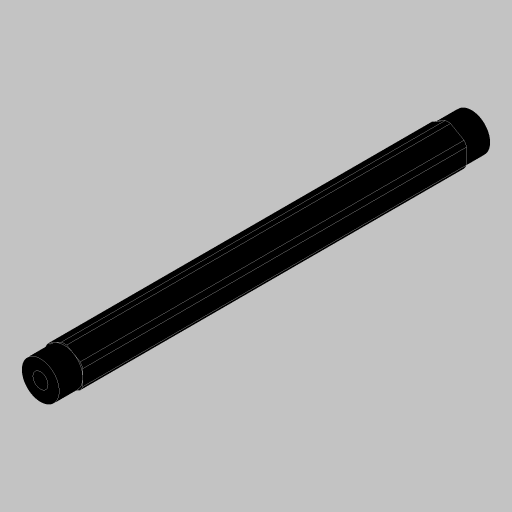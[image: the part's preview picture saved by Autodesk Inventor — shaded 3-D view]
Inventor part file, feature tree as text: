
AUTODESK INVENTOR PART (.ipt)
format: ipt  version: 2023.5 (Build 275446000, 446)  size: 162,304 bytes
history: native  units: in
note: dims shown in document units (in); Inventor stores cm internally (conversion verified against a paired STEP export)
features: extrude x3, projected_geometry x3, hole x1, mirror x1, sketch x1
ambient origin geometry x8: Origin, YZ Plane, XZ Plane, XY Plane, X Axis, Y Axis, Z Axis, Center Point
bodies: Solid1 (feature_tree)
feature tree (9):
  extrude  "Extrusion1"  Depth=0.315in
  hole  "Hole1"  [1 undecoded]
  extrude  "Extrusion3"  Depth=0.5in
  extrude  "Extrusion4"  Depth=0.315in TaperAngle=0.0deg
  mirror  "Mirror2"
  sketch  "Sketch5"  dims[d2=0.0in d9=0.625in d10=0.385in d11=0.25in d12=0.5635in d13=1.0in d14=0.8108in d16=0.7in d17=0.0in d18=0.0in d19=0.5in d20=0.315in d21=0.0in]
  projected_geometry  "Project Cut Edges1"
  projected_geometry  "Project Cut Edges2"
  projected_geometry  "Project Cut Edges3"
note: 1 required parameter value undecoded (feature->parameter linkage not recoverable at this tier; creation-order binding heuristic only, values carry confidence <= 0.55)
